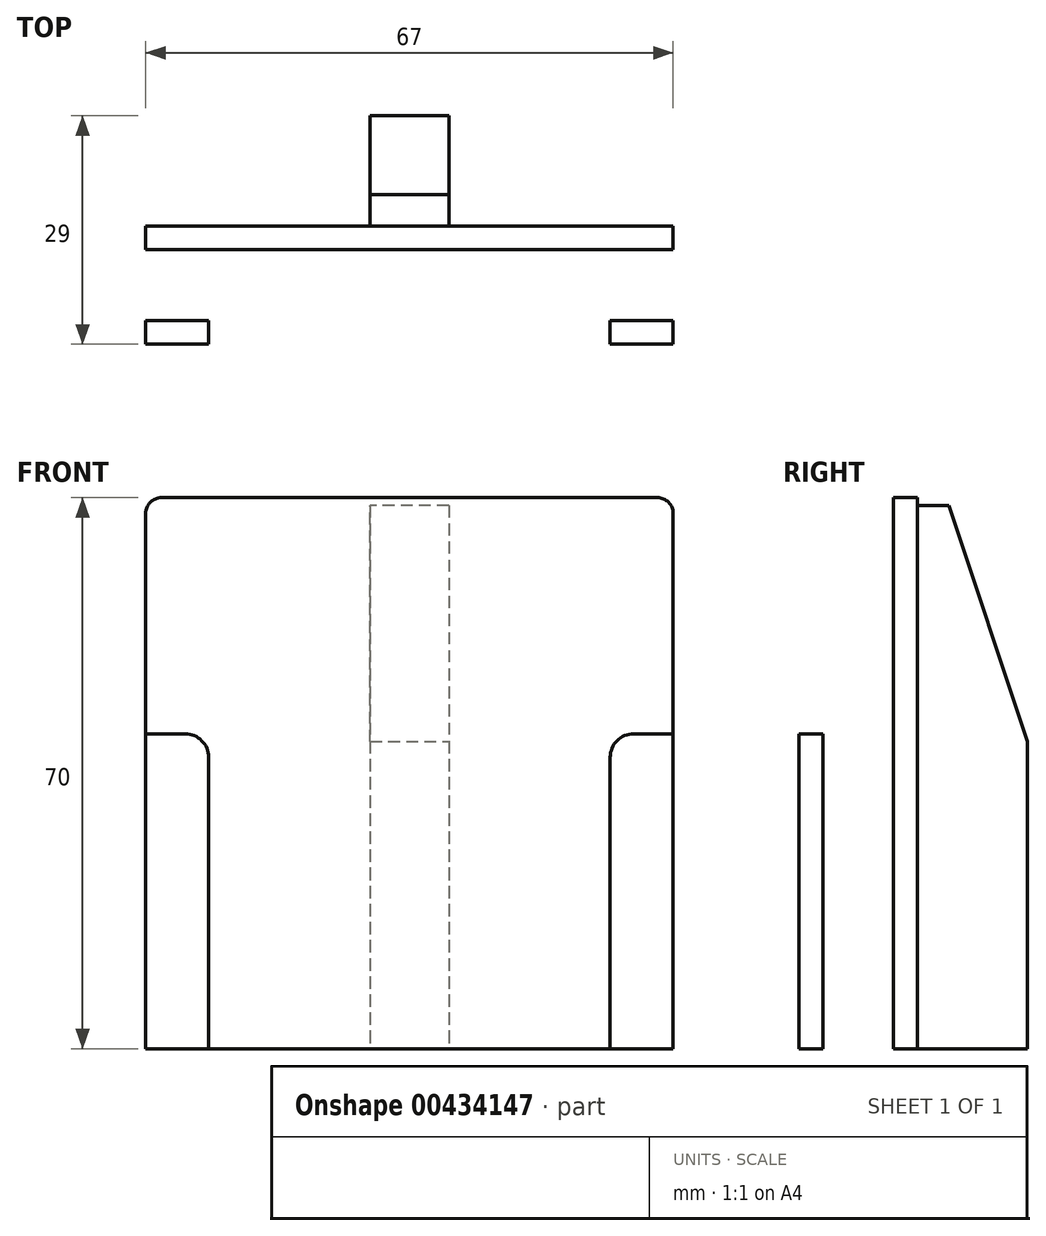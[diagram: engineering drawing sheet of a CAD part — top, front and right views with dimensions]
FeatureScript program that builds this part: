
annotation { "Feature Type Name" : "Feature", "Feature Type Description" : "" }
export const myFeature = defineFeature(function(context is Context, id is Id, definition is map)
    precondition{}
    {
        {
            var Q0;
            Q0=qCreatedBy(makeId("Top.planeOp"),FACE);
            var sketch = newSketch(context, id + "F0", { "sketchPlane" : qUnion([Q0])});
            skLineSegment(sketch, "E0.bottom", {"start": v(33.5, 23.76) * mm, "end": v(-33.5, 23.76) * mm});
            skLineSegment(sketch, "E0.top", {"start": v(33.5, 20.76) * mm, "end": v(-33.5, 20.76) * mm});
            skLineSegment(sketch, "E0.left", {"start": v(33.5, 23.76) * mm, "end": v(33.5, 20.76) * mm});
            skLineSegment(sketch, "E0.right", {"start": v(-33.5, 23.76) * mm, "end": v(-33.5, 20.76) * mm});
            skPoint(sketch, "E0.middle", {"position": v(0, 22.26) * mm});
            skLineSegment(sketch, "E1.bottom", {"start": v(-33.5, 20.76) * mm, "end": v(-30.5, 20.76) * mm});
            skLineSegment(sketch, "E1.top", {"start": v(-33.5, 11.76) * mm, "end": v(-30.5, 11.76) * mm});
            skLineSegment(sketch, "E1.left", {"start": v(-33.5, 20.76) * mm, "end": v(-33.5, 11.76) * mm});
            skLineSegment(sketch, "E1.right", {"start": v(-30.5, 20.76) * mm, "end": v(-30.5, 11.76) * mm});
            skLineSegment(sketch, "E2.bottom", {"start": v(33.5, 23.76) * mm, "end": v(32.5, 23.76) * mm});
            skLineSegment(sketch, "E3.bottom", {"start": v(-33.5, 11.76) * mm, "end": v(-25.5, 11.76) * mm});
            skLineSegment(sketch, "E3.top", {"start": v(-33.5, 8.76) * mm, "end": v(-25.5, 8.76) * mm});
            skLineSegment(sketch, "E3.left", {"start": v(-33.5, 11.76) * mm, "end": v(-33.5, 8.76) * mm});
            skLineSegment(sketch, "E3.right", {"start": v(-25.5, 11.76) * mm, "end": v(-25.5, 8.76) * mm});
            skLineSegment(sketch, "E4.bottom", {"start": v(33.5, 20.76) * mm, "end": v(30.5, 20.76) * mm});
            skLineSegment(sketch, "E4.top", {"start": v(33.5, 11.76) * mm, "end": v(30.5, 11.76) * mm});
            skLineSegment(sketch, "E4.left", {"start": v(33.5, 20.76) * mm, "end": v(33.5, 11.76) * mm});
            skLineSegment(sketch, "E4.right", {"start": v(30.5, 20.76) * mm, "end": v(30.5, 11.76) * mm});
            skLineSegment(sketch, "E5.bottom", {"start": v(33.5, 11.76) * mm, "end": v(25.5, 11.76) * mm});
            skLineSegment(sketch, "E5.top", {"start": v(33.5, 8.76) * mm, "end": v(25.5, 8.76) * mm});
            skLineSegment(sketch, "E5.left", {"start": v(33.5, 11.76) * mm, "end": v(33.5, 8.76) * mm});
            skLineSegment(sketch, "E5.right", {"start": v(25.5, 11.76) * mm, "end": v(25.5, 8.76) * mm});
            skLineSegment(sketch, "E6.bottom", {"start": v(-5, 22.76) * mm, "end": v(5, 22.76) * mm});
            skLineSegment(sketch, "E6.top", {"start": v(-5, 37.76) * mm, "end": v(5, 37.76) * mm});
            skLineSegment(sketch, "E6.left", {"start": v(-5, 22.76) * mm, "end": v(-5, 37.76) * mm});
            skLineSegment(sketch, "E6.right", {"start": v(5, 22.76) * mm, "end": v(5, 37.76) * mm});
            skPoint(sketch, "E6.middle", {"position": v(0, 30.26) * mm});
            skSolve(sketch);
        }
        {
            var Q0;
            Q0=makeQuery(id+"F0.imprint","IMPRINT",FACE,{"disambiguationData":[TD([[makeQuery(id+"F0.imprint","IMPRINT",EDGE,{"derivedFrom":sQuery(id+"F0.wireOp",EDGE,"E0.top")}),-1.0]])]});
            var Q1;
            {var subQ5=sQuery(id+"F0.wireOp",EDGE,"E6.bottom");Q1=makeQuery(id+"F0.imprint","IMPRINT",FACE,{"disambiguationData":[TD([[makeQuery(id+"F0.imprint","IMPRINT",EDGE,{"derivedFrom":subQ5}),1.0]])]});}
            extrude(context, id + "F1", {"entities" : qUnion([Q0, Q1]), "depth" : 70 * mm, "offsetDistance" : 25 * mm});
        }
        {
            var Q0;
            Q0=makeQuery(id+"F0.imprint","IMPRINT",FACE,{"disambiguationData":[TD([[makeQuery(id+"F0.imprint","IMPRINT",EDGE,{"derivedFrom":sQuery(id+"F0.wireOp",EDGE,"E3.top")}),1.0]])]});
            var Q1;
            Q1=makeQuery(id+"F0.imprint","IMPRINT",FACE,{"disambiguationData":[TD([[makeQuery(id+"F0.imprint","IMPRINT",EDGE,{"derivedFrom":sQuery(id+"F0.wireOp",EDGE,"E1.bottom")}),-1.0]])]});
            var Q2;
            Q2=makeQuery(id+"F0.imprint","IMPRINT",FACE,{"disambiguationData":[TD([[makeQuery(id+"F0.imprint","IMPRINT",EDGE,{"derivedFrom":sQuery(id+"F0.wireOp",EDGE,"E5.top")}),-1.0]])]});
            var Q3;
            Q3=makeQuery(id+"F0.imprint","IMPRINT",FACE,{"disambiguationData":[TD([[makeQuery(id+"F0.imprint","IMPRINT",EDGE,{"derivedFrom":sQuery(id+"F0.wireOp",EDGE,"E4.bottom")}),1.0]])]});
            extrude(context, id + "F2", {"entities" : qUnion([Q0, Q1, Q2, Q3]), "operationType" : NewBodyOperationType.ADD, "depth" : 40 * mm});
        }
        {
            var Q0;
            Q0=makeQuery(id+"F1.opExtrude","CAP_EDGE",EDGE,{"disambiguationData":[OSD([sQuery(id+"F0.wireOp",EDGE,"E0.left")])],"isStart":false});
            var Q1;
            Q1=makeQuery(id+"F1.opExtrude","CAP_EDGE",EDGE,{"disambiguationData":[OSD([sQuery(id+"F0.wireOp",EDGE,"E0.right")])],"isStart":false});
            fillet(context, id + "F3", {"entities" : qUnion([Q0, Q1]), "radius" : 2 * mm, "tangentPropagation" : true, "allowEdgeOverflow" : false});
        }
        {
            var Q0;
            Q0=makeQuery(id+"F2.opExtrude","CAP_EDGE",EDGE,{"disambiguationData":[OSD([sQuery(id+"F0.wireOp",EDGE,"E5.right")])],"isStart":false});
            var Q1;
            Q1=makeQuery(id+"F2.opExtrude","CAP_EDGE",EDGE,{"disambiguationData":[OSD([sQuery(id+"F0.wireOp",EDGE,"E3.right")])],"isStart":false});
            fillet(context, id + "F4", {"entities" : qUnion([Q0, Q1]), "radius" : 3 * mm, "tangentPropagation" : true, "allowEdgeOverflow" : false});
        }
        {
            var Q0;
            {var subQ5=sQuery(id+"F0.wireOp",EDGE,"E6.top");Q0=makeQuery(id+"F0.imprint","IMPRINT",FACE,{"disambiguationData":[TD([[makeQuery(id+"F0.imprint","IMPRINT",EDGE,{"derivedFrom":subQ5}),-1.0]])]});}
            extrude(context, id + "F5", {"entities" : qUnion([Q0]), "operationType" : NewBodyOperationType.ADD, "depth" : 69 * mm, "offsetDistance" : 25 * mm});
        }
        {
            var Q0;
            Q0=makeQuery(id+"F5.opExtrude","CAP_EDGE",EDGE,{"disambiguationData":[OSD([sQuery(id+"F0.wireOp",EDGE,"E6.top")])],"isStart":false});
            chamfer(context, id + "F6", {"entities" : qUnion([Q0]), "chamferType" : ChamferType.TWO_OFFSETS, "width1" : 30 * mm, "oppositeDirection" : false, "width2" : 10 * mm, "tangentPropagation" : true});
        }
    });
